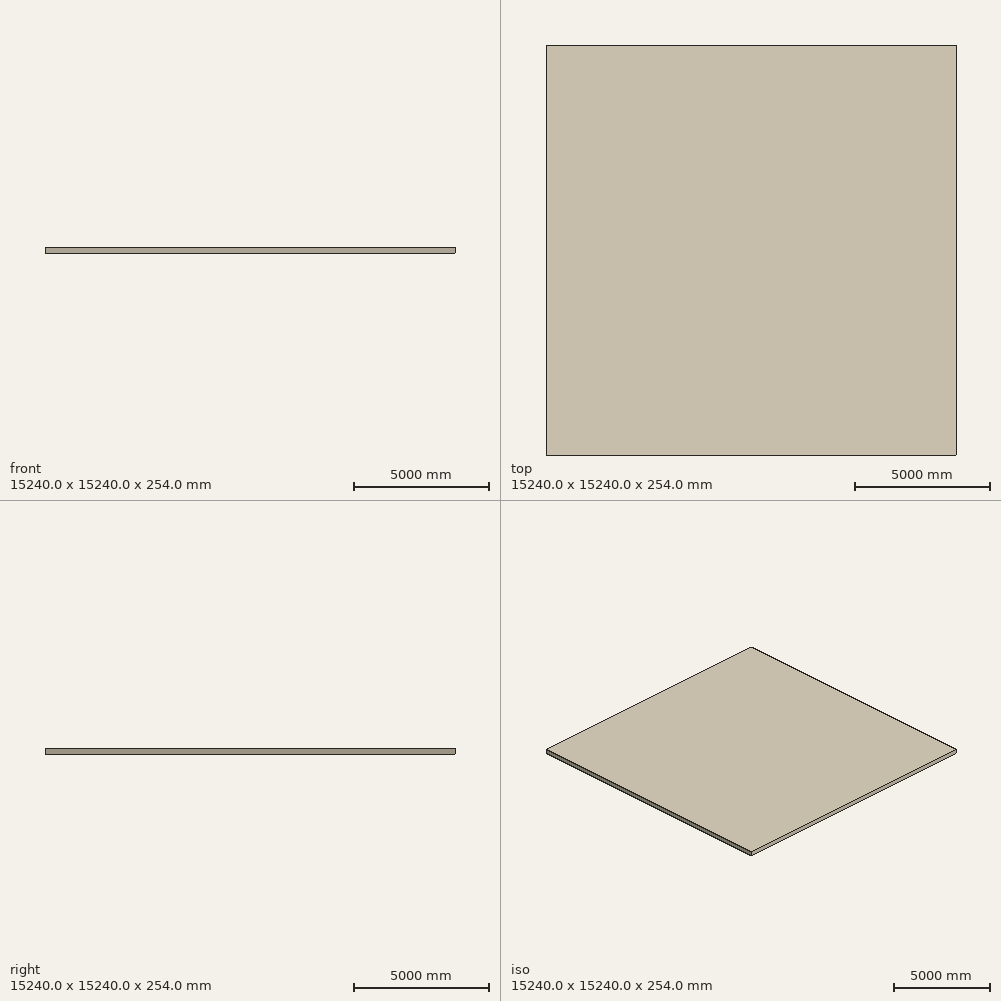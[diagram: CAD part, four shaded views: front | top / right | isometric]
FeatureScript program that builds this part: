
annotation { "Feature Type Name" : "Feature", "Feature Type Description" : "" }
export const myFeature = defineFeature(function(context is Context, id is Id, definition is map)
    precondition{}
    {
        {
            var Q0;
            Q0=qCreatedBy(makeId("Top.planeOp"),FACE);
            var sketch = newSketch(context, id + "F0", { "sketchPlane" : qUnion([Q0])});
            skLineSegment(sketch, "E0.bottom", {"start": v(7620, 7620) * mm, "end": v(-7620, 7620) * mm});
            skLineSegment(sketch, "E0.top", {"start": v(7620, -7620) * mm, "end": v(-7620, -7620) * mm});
            skLineSegment(sketch, "E0.left", {"start": v(7620, 7620) * mm, "end": v(7620, -7620) * mm});
            skLineSegment(sketch, "E0.right", {"start": v(-7620, 7620) * mm, "end": v(-7620, -7620) * mm});
            skPoint(sketch, "E0.middle", {"position": v(0, 0) * mm});
            skSolve(sketch);
        }
        {
            var Q0;
            Q0=makeQuery(id+"F0.imprint","IMPRINT",FACE,{"disambiguationData":[TD([[makeQuery(id+"F0.imprint","IMPRINT",EDGE,{"derivedFrom":sQuery(id+"F0.wireOp",EDGE,"E0.bottom")}),1.0]])]});
            extrude(context, id + "F1", {"entities" : qUnion([Q0]), "oppositeDirection" : true, "depth" : 254 * mm});
        }
    });
